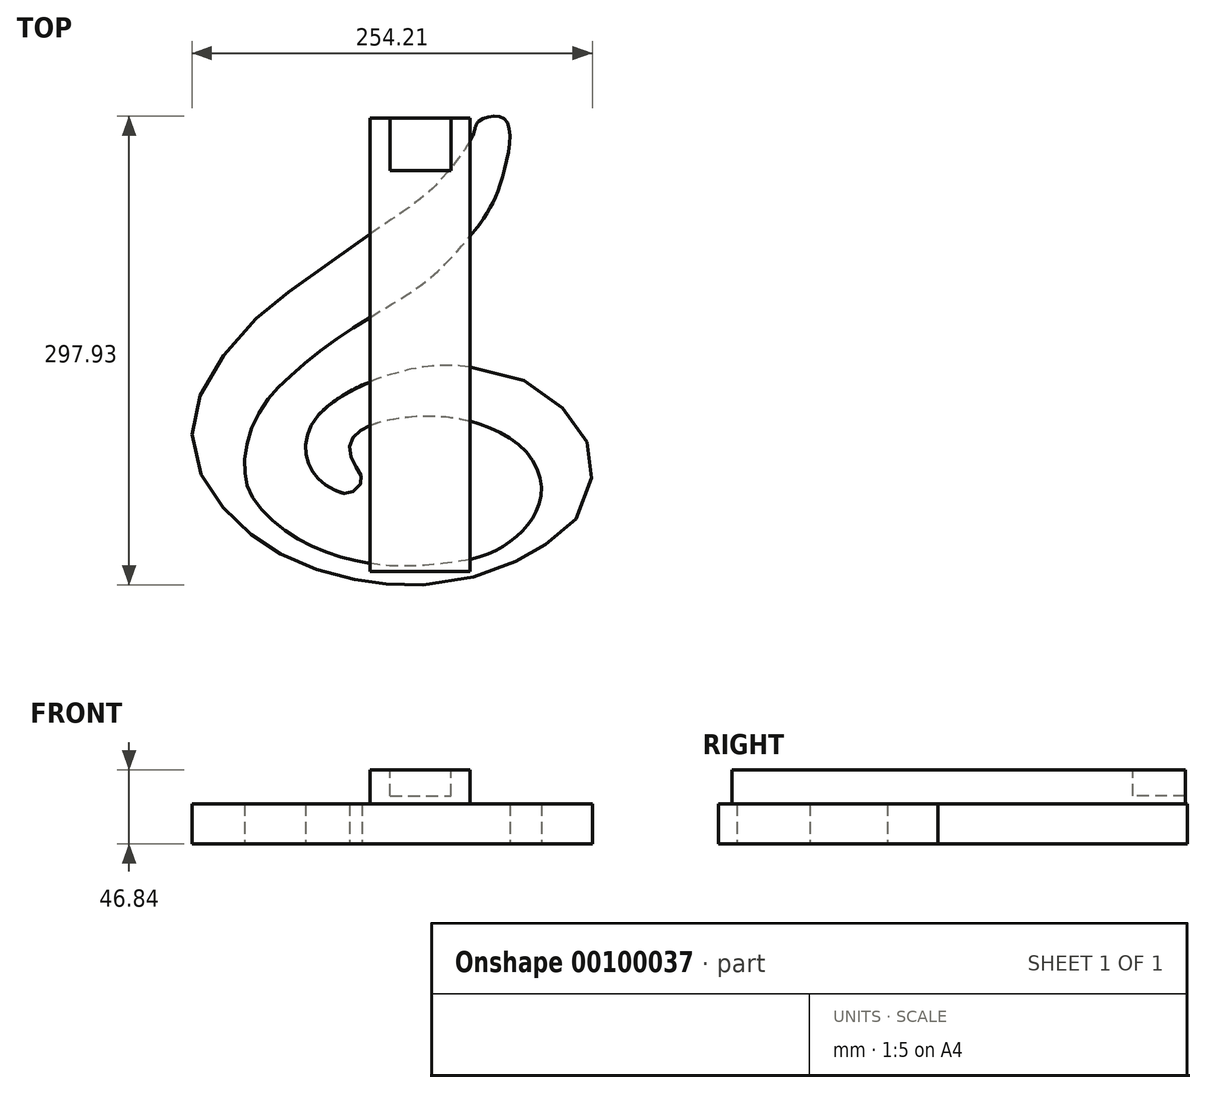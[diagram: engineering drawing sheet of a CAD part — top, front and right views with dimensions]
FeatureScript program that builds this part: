
annotation { "Feature Type Name" : "Feature", "Feature Type Description" : "" }
export const myFeature = defineFeature(function(context is Context, id is Id, definition is map)
    precondition{}
    {
        {
            var Q0;
            Q0=qCreatedBy(makeId("Top.planeOp"),FACE);
            var sketch = newSketch(context, id + "F0", { "sketchPlane" : qUnion([Q0])});
            skFitSpline(sketch, "E0", {"points": [v(30.5, 170.07) * mm, v(27.25, 162.63) * mm, v(21.88, 152.87) * mm, v(15.36, 143.54) * mm, v(4.68, 131.3) * mm, v(-1.55, 124.97) * mm, v(-15.18, 114.49) * mm, v(-31.89, 103.02) * mm, v(-46.45, 92.93) * mm, v(-82.16, 67.45) * mm, v(-103.66, 51.5) * mm, v(-126.32, 28.2) * mm, v(-144.74, 0) * mm, v(-151.54, -22.45) * mm, v(-148.68, -46.93) * mm, v(-138.56, -66.9) * mm, v(-123, -84.7) * mm, v(-107.61, -97.51) * mm, v(-91.89, -106.69) * mm, v(-70.6, -115.35) * mm, v(-49.06, -120.96) * mm, v(-33.54, -123.4) * mm, v(-18.67, -124.47) * mm, v(9.73, -123.2) * mm, v(46.23, -113.04) * mm, v(62.1, -105.36) * mm, v(78.37, -94.97) * mm, v(95.35, -77.48) * mm, v(102.46, -50.83) * mm, v(98.88, -33.44) * mm, v(83.7, -12.17) * mm, v(56.57, 6.2) * mm, v(12.84, 14.88) * mm, v(-18.26, 11.11) * mm, v(-48.43, 0) * mm, v(-70.85, -15.91) * mm, v(-78.4, -28.97) * mm, v(-79.38, -40.16) * mm, v(-76.91, -49.59) * mm, v(-71.3, -57.44) * mm, v(-61.42, -64.18) * mm, v(-51.1, -65.97) * mm, v(-43.91, -57.9) * mm, v(-48.4, -48.24) * mm, v(-51.55, -35.44) * mm, v(-44.81, -26.46) * mm, v(-30.9, -20.63) * mm, v(-11.59, -17.56) * mm, v(7.45, -17.5) * mm, v(32.03, -22.76) * mm, v(60.74, -40.35) * mm, v(70.15, -64.08) * mm, v(64.52, -82.16) * mm, v(52.35, -95.39) * mm, v(34.31, -105.66) * mm, v(8.21, -110.94) * mm, v(-19.6, -112.65) * mm, v(-41.05, -110.54) * mm, v(-61.75, -105.33) * mm, v(-81.89, -96.71) * mm, v(-100.36, -83.93) * mm, v(-114, -67.46) * mm, v(-118.23, -53.36) * mm, v(-116.54, -33.32) * mm, v(-105.93, -9.9) * mm, v(-89.74, 7.88) * mm, v(-62.09, 30.05) * mm, v(-31.38, 49.83) * mm, v(-6.38, 65.81) * mm, v(10.77, 81.1) * mm, v(33.96, 109.06) * mm, v(45.35, 134.6) * mm, v(46.88, 171.17) * mm, v(30.5, 170.07) * mm]});
            skPoint(sketch, "E1", {"position": v(29.4, 168.9) * mm});
            skPoint(sketch, "E2", {"position": v(34.31, -117.24) * mm});
            skSolve(sketch);
        }
        {
            var Q0;
            Q0=qSketchRegion(id+"F0",true);
            extrude(context, id + "F1", {"entities" : qUnion([Q0]), "depth" : 25.4 * mm});
        }
        {
            var Q0;
            Q0=makeQuery(id+"F1.opExtrude","CAP_FACE",FACE,{"disambiguationData":[OSD([sQuery(id+"F0.wireOp",EDGE,"E0")])],"isStart":false});
            var sketch = newSketch(context, id + "F2", { "sketchPlane" : qUnion([Q0])});
            skLineSegment(sketch, "E3.bottom", {"start": v(24.8, -12.84) * mm, "end": v(-38.7, -12.84) * mm});
            skLineSegment(sketch, "E3.top", {"start": v(24.8, 634.86) * mm, "end": v(-38.7, 634.86) * mm});
            skLineSegment(sketch, "E3.left", {"start": v(24.8, -12.84) * mm, "end": v(24.8, 634.86) * mm});
            skLineSegment(sketch, "E3.right", {"start": v(-38.7, -12.84) * mm, "end": v(-38.7, 634.86) * mm});
            skLineSegment(sketch, "E4.bottom", {"start": v(-38.7, -12.84) * mm, "end": v(22.52, -12.84) * mm});
            skPoint(sketch, "E5", {"position": v(-38.7, -116.1) * mm});
            skLineSegment(sketch, "E6", {"start": v(-38.7, -12.84) * mm, "end": v(-38.7, -116.1) * mm});
            skLineSegment(sketch, "E7", {"start": v(24.8, -12.84) * mm, "end": v(24.8, -115.97) * mm});
            skLineSegment(sketch, "E8", {"start": v(24.8, -115.97) * mm, "end": v(-38.7, -116.1) * mm});
            skPoint(sketch, "E9", {"position": v(24.8, 171.87) * mm});
            skPoint(sketch, "E10", {"position": v(-38.7, 171.87) * mm});
            skLineSegment(sketch, "E11", {"start": v(-38.7, 171.87) * mm, "end": v(24.8, 171.87) * mm});
            skSolve(sketch);
        }
        {
            var Q0;
            {var subQ0=sQuery(id+"F2.wireOp",EDGE,"E11");Q0=makeQuery(id+"F2.imprint","IMPRINT",FACE,{"disambiguationData":[TD([[makeQuery(id+"F2.imprint","IMPRINT",EDGE,{"derivedFrom":subQ0}),-1.0]])]});}
            var Q1;
            {var subQ0=sQuery(id+"F2.wireOp",EDGE,"E3.left");var subQ1=makeQuery(id+"F1.opExtrude","CAP_EDGE",EDGE,{"disambiguationData":[OSD([sQuery(id+"F0.wireOp",EDGE,"E0")])],"isStart":false});var subQ2=makeQuery(id+"F2.imprint","INTERSECT",VERTEX,{"disambiguationData":[OD(1.0)],"derivedFrom":[subQ1,subQ0]});Q1=makeQuery(id+"F2.imprint","IMPRINT",FACE,{"disambiguationData":[TD([[makeQuery(id+"F2.imprint","IMPRINT",EDGE,{"disambiguationData":[TD([[subQ2,-1.0]])],"derivedFrom":subQ0}),1.0]])]});}
            var Q2;
            {var subQ6=sQuery(id+"F2.wireOp",EDGE,"E3.bottom");Q2=makeQuery(id+"F2.imprint","IMPRINT",FACE,{"disambiguationData":[TD([[makeQuery(id+"F2.imprint","IMPRINT",EDGE,{"derivedFrom":subQ6}),-1.0]])]});}
            var Q3;
            {var subQ1=sQuery(id+"F2.wireOp",EDGE,"E3.bottom");Q3=makeQuery(id+"F2.imprint","IMPRINT",FACE,{"disambiguationData":[TD([[makeQuery(id+"F2.imprint","IMPRINT",EDGE,{"derivedFrom":subQ1}),1.0]])]});}
            var Q4;
            {var subQ0=sQuery(id+"F2.wireOp",EDGE,"E8");Q4=makeQuery(id+"F2.imprint","IMPRINT",FACE,{"disambiguationData":[TD([[makeQuery(id+"F2.imprint","IMPRINT",EDGE,{"derivedFrom":subQ0}),-1.0]])]});}
            var Q5;
            {var subQ0=sQuery(id+"F2.wireOp",EDGE,"E6");var subQ1=makeQuery(id+"F1.opExtrude","CAP_EDGE",EDGE,{"disambiguationData":[OSD([sQuery(id+"F0.wireOp",EDGE,"E0")])],"isStart":false});var subQ2=makeQuery(id+"F2.imprint","INTERSECT",VERTEX,{"disambiguationData":[OD(1.0)],"derivedFrom":[subQ1,subQ0]});Q5=makeQuery(id+"F2.imprint","IMPRINT",FACE,{"disambiguationData":[TD([[makeQuery(id+"F2.imprint","IMPRINT",EDGE,{"disambiguationData":[TD([[subQ2,-1.0]])],"derivedFrom":subQ0}),1.0]])]});}
            var Q6;
            {var subQ1=makeQuery(id+"F1.opExtrude","CAP_EDGE",EDGE,{"disambiguationData":[OSD([sQuery(id+"F0.wireOp",EDGE,"E0")])],"isStart":false});var subQ4=sQuery(id+"F2.wireOp",EDGE,"E6");var subQ8=makeQuery(id+"F2.imprint","INTERSECT",VERTEX,{"disambiguationData":[OD(0.0)],"derivedFrom":[subQ1,subQ4]});Q6=makeQuery(id+"F2.imprint","IMPRINT",FACE,{"disambiguationData":[TD([[makeQuery(id+"F2.imprint","IMPRINT",EDGE,{"disambiguationData":[TD([[subQ8,-1.0]])],"derivedFrom":subQ4}),1.0]])]});}
            var Q7;
            {var subQ0=sQuery(id+"F2.wireOp",EDGE,"E3.left");var subQ1=makeQuery(id+"F1.opExtrude","CAP_EDGE",EDGE,{"disambiguationData":[OSD([sQuery(id+"F0.wireOp",EDGE,"E0")])],"isStart":false});var subQ2=makeQuery(id+"F2.imprint","INTERSECT",VERTEX,{"disambiguationData":[OD(0.0)],"derivedFrom":[subQ1,subQ0]});Q7=makeQuery(id+"F2.imprint","IMPRINT",FACE,{"disambiguationData":[TD([[makeQuery(id+"F2.imprint","IMPRINT",EDGE,{"disambiguationData":[TD([[subQ2,-1.0]])],"derivedFrom":subQ0}),1.0]])]});}
            extrude(context, id + "F3", {"entities" : qUnion([Q0, Q1, Q2, Q3, Q4, Q5, Q6, Q7]), "operationType" : NewBodyOperationType.ADD, "depth" : 21.44 * mm});
        }
        {
            var Q0;
            Q0=makeQuery(id+"F3.opExtrude","CAP_FACE",FACE,{"disambiguationData":[OSD([sQuery(id+"F2.wireOp",EDGE,"E3.left"),sQuery(id+"F2.wireOp",EDGE,"E3.right"),sQuery(id+"F2.wireOp",EDGE,"E6"),sQuery(id+"F2.wireOp",EDGE,"E7"),sQuery(id+"F2.wireOp",EDGE,"E8"),sQuery(id+"F2.wireOp",EDGE,"E11")])],"isStart":false});
            var sketch = newSketch(context, id + "F4", { "sketchPlane" : qUnion([Q0])});
            skLineSegment(sketch, "E12", {"start": v(12.1, 184.28) * mm, "end": v(-26, 184.28) * mm});
            skLineSegment(sketch, "E13.bottom", {"start": v(-26, 184.28) * mm, "end": v(12.66, 184.28) * mm});
            skLineSegment(sketch, "E13.top", {"start": v(-26, 138.51) * mm, "end": v(12.66, 138.51) * mm});
            skLineSegment(sketch, "E13.left", {"start": v(-26, 184.28) * mm, "end": v(-26, 138.51) * mm});
            skLineSegment(sketch, "E13.right", {"start": v(12.66, 184.28) * mm, "end": v(12.66, 138.51) * mm});
            skSolve(sketch);
        }
        {
            var Q0;
            {var subQ0=sQuery(id+"F4.wireOp",EDGE,"E13.top");Q0=makeQuery(id+"F4.imprint","IMPRINT",FACE,{"disambiguationData":[TD([[makeQuery(id+"F4.imprint","IMPRINT",EDGE,{"derivedFrom":subQ0}),1.0]])]});}
            extrude(context, id + "F5", {"entities" : qUnion([Q0]), "operationType" : NewBodyOperationType.REMOVE, "oppositeDirection" : true, "depth" : 16.38 * mm});
        }
    });
